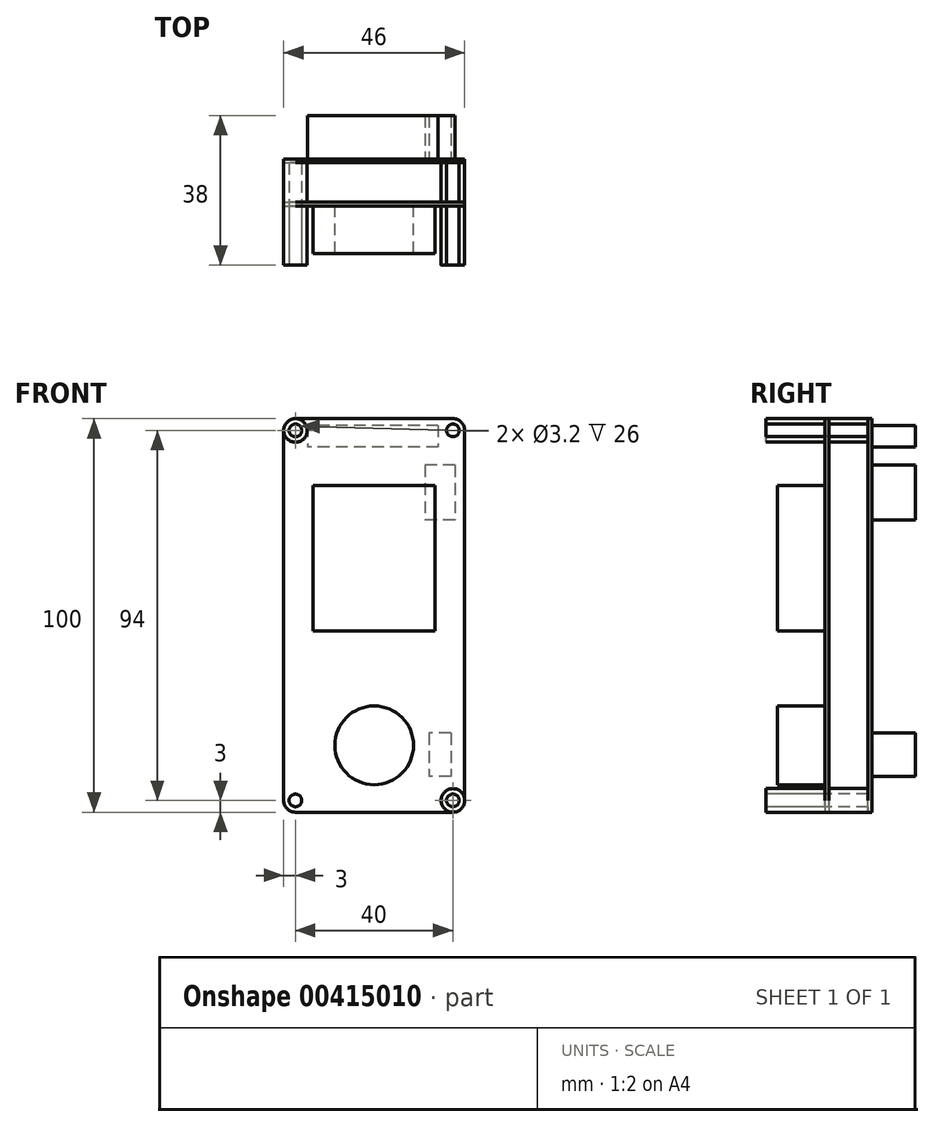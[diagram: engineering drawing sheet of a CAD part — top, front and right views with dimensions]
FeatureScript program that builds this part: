
annotation { "Feature Type Name" : "Feature", "Feature Type Description" : "" }
export const myFeature = defineFeature(function(context is Context, id is Id, definition is map)
    precondition{}
    {
        {
            var Q0;
            Q0=qCreatedBy(makeId("Front.planeOp"),FACE);
            var sketch = newSketch(context, id + "F0", { "sketchPlane" : qUnion([Q0])});
            skLineSegment(sketch, "E0.bottom", {"start": v(20, 50) * mm, "end": v(-20, 50) * mm});
            skLineSegment(sketch, "E0.top", {"start": v(20, -50) * mm, "end": v(-20, -50) * mm});
            skLineSegment(sketch, "E0.left", {"start": v(23, 47) * mm, "end": v(23, -47) * mm});
            skLineSegment(sketch, "E0.right", {"start": v(-23, 47) * mm, "end": v(-23, -47) * mm});
            skPoint(sketch, "E0.middle", {"position": v(0, 0) * mm});
            skPoint(sketch, "E1.visualSharp", {"position": v(-23, 50) * mm});
            skArc(sketch, "E1.filletArc", {"start": v(-20, 50) * mm, "mid": v(-22.12, 49.12) * mm, "end": v(-23, 47) * mm});
            skPoint(sketch, "E2.visualSharp", {"position": v(23, 50) * mm});
            skArc(sketch, "E2.filletArc", {"start": v(23, 47) * mm, "mid": v(22.12, 49.12) * mm, "end": v(20, 50) * mm});
            skPoint(sketch, "E3.visualSharp", {"position": v(23, -50) * mm});
            skArc(sketch, "E3.filletArc", {"start": v(20, -50) * mm, "mid": v(22.12, -49.12) * mm, "end": v(23, -47) * mm});
            skPoint(sketch, "E4.visualSharp", {"position": v(-23, -50) * mm});
            skArc(sketch, "E4.filletArc", {"start": v(-23, -47) * mm, "mid": v(-22.12, -49.12) * mm, "end": v(-20, -50) * mm});
            skCircle(sketch, "E5", {"center": v(-20, 47) * mm, "radius": 1.6 * mm});
            skCircle(sketch, "E6.MirrorC", {"center": v(20, 47) * mm, "radius": 1.6 * mm});
            skCircle(sketch, "E7.MirrorC", {"center": v(-20, -47) * mm, "radius": 1.6 * mm});
            skCircle(sketch, "E8.MirrorC", {"center": v(20, -47) * mm, "radius": 1.6 * mm});
            skLineSegment(sketch, "E9.bottom", {"start": v(-15.5, 33) * mm, "end": v(15.5, 33) * mm});
            skLineSegment(sketch, "E9.top", {"start": v(-15.5, -4) * mm, "end": v(15.5, -4) * mm});
            skLineSegment(sketch, "E9.left", {"start": v(-15.5, 33) * mm, "end": v(-15.5, -4) * mm});
            skLineSegment(sketch, "E9.right", {"start": v(15.5, 33) * mm, "end": v(15.5, -4) * mm});
            skPoint(sketch, "E9.middle", {"position": v(0, 14.5) * mm});
            skCircle(sketch, "E10", {"center": v(0, -33) * mm, "radius": 10 * mm});
            skSolve(sketch);
        }
        {
            var Q0;
            Q0=makeQuery(id+"F0.imprint","IMPRINT",FACE,{"disambiguationData":[TD([[makeQuery(id+"F0.imprint","IMPRINT",EDGE,{"derivedFrom":sQuery(id+"F0.wireOp",EDGE,"E0.bottom")}),1.0]])]});
            var Q1;
            Q1=makeQuery(id+"F0.imprint","IMPRINT",FACE,{"disambiguationData":[TD([[makeQuery(id+"F0.imprint","IMPRINT",EDGE,{"derivedFrom":sQuery(id+"F0.wireOp",EDGE,"E9.bottom")}),-1.0]])]});
            var Q2;
            Q2=makeQuery(id+"F0.imprint","IMPRINT",FACE,{"disambiguationData":[TD([[makeQuery(id+"F0.imprint","IMPRINT",EDGE,{"derivedFrom":sQuery(id+"F0.wireOp",EDGE,"E10")}),1.0]])]});
            extrude(context, id + "F1", {"entities" : qUnion([Q0, Q1, Q2]), "oppositeDirection" : true, "depth" : 1 * mm});
        }
        {
            var Q0;
            Q0=makeQuery(id+"F0.imprint","IMPRINT",FACE,{"disambiguationData":[TD([[makeQuery(id+"F0.imprint","IMPRINT",EDGE,{"derivedFrom":sQuery(id+"F0.wireOp",EDGE,"E9.bottom")}),-1.0]])]});
            var Q1;
            Q1=makeQuery(id+"F0.imprint","IMPRINT",FACE,{"disambiguationData":[TD([[makeQuery(id+"F0.imprint","IMPRINT",EDGE,{"derivedFrom":sQuery(id+"F0.wireOp",EDGE,"E10")}),1.0]])]});
            extrude(context, id + "F2", {"entities" : qUnion([Q0, Q1]), "operationType" : NewBodyOperationType.ADD, "depth" : 12 * mm});
        }
        {
            var Q0;
            Q0=makeQuery(id+"F1.opExtrude","CAP_FACE",FACE,{"disambiguationData":[OSD([sQuery(id+"F0.wireOp",EDGE,"E0.bottom"),sQuery(id+"F0.wireOp",EDGE,"E0.top"),sQuery(id+"F0.wireOp",EDGE,"E0.left"),sQuery(id+"F0.wireOp",EDGE,"E0.right"),sQuery(id+"F0.wireOp",EDGE,"E1.filletArc"),sQuery(id+"F0.wireOp",EDGE,"E2.filletArc"),sQuery(id+"F0.wireOp",EDGE,"E3.filletArc"),sQuery(id+"F0.wireOp",EDGE,"E4.filletArc"),sQuery(id+"F0.wireOp",EDGE,"E5"),sQuery(id+"F0.wireOp",EDGE,"E6.MirrorC"),sQuery(id+"F0.wireOp",EDGE,"E7.MirrorC"),sQuery(id+"F0.wireOp",EDGE,"E8.MirrorC")])],"isStart":false});
            var sketch = newSketch(context, id + "F3", { "sketchPlane" : qUnion([Q0])});
            skCircle(sketch, "E11.0", {"center": v(-20, 47) * mm, "radius": 1.6 * mm});
            skArc(sketch, "E12.0", {"start": v(-23, 47) * mm, "mid": v(-22.12, 49.12) * mm, "end": v(-20, 50) * mm});
            skCircle(sketch, "E13.0", {"center": v(20, 47) * mm, "radius": 1.6 * mm});
            skArc(sketch, "E14.0", {"start": v(20, 50) * mm, "mid": v(22.12, 49.12) * mm, "end": v(23, 47) * mm});
            skCircle(sketch, "E15.0", {"center": v(20, -47) * mm, "radius": 1.6 * mm});
            skArc(sketch, "E16.0", {"start": v(23, -47) * mm, "mid": v(22.12, -49.12) * mm, "end": v(20, -50) * mm});
            skCircle(sketch, "E17.0", {"center": v(-20, -47) * mm, "radius": 1.6 * mm});
            skArc(sketch, "E18.0", {"start": v(-20, -50) * mm, "mid": v(-22.12, -49.12) * mm, "end": v(-23, -47) * mm});
            skCircle(sketch, "E19", {"center": v(-20, -47) * mm, "radius": 3 * mm});
            skCircle(sketch, "E20", {"center": v(20, -47) * mm, "radius": 3 * mm});
            skCircle(sketch, "E21", {"center": v(-20, 47) * mm, "radius": 3 * mm});
            skCircle(sketch, "E22", {"center": v(20, 47) * mm, "radius": 3 * mm});
            skSolve(sketch);
        }
        {
            var Q0;
            Q0=makeQuery(id+"F3.imprint","IMPRINT",FACE,{"disambiguationData":[TD([[makeQuery(id+"F3.imprint","IMPRINT",EDGE,{"derivedFrom":sQuery(id+"F3.wireOp",EDGE,"E11.0")}),-1.0]])]});
            var Q1;
            Q1=makeQuery(id+"F3.imprint","IMPRINT",FACE,{"disambiguationData":[TD([[makeQuery(id+"F3.imprint","IMPRINT",EDGE,{"derivedFrom":sQuery(id+"F3.wireOp",EDGE,"E13.0")}),1.0]])]});
            var Q2;
            Q2=makeQuery(id+"F3.imprint","IMPRINT",FACE,{"disambiguationData":[TD([[makeQuery(id+"F3.imprint","IMPRINT",EDGE,{"derivedFrom":sQuery(id+"F3.wireOp",EDGE,"E15.0")}),-1.0]])]});
            var Q3;
            Q3=makeQuery(id+"F3.imprint","IMPRINT",FACE,{"disambiguationData":[TD([[makeQuery(id+"F3.imprint","IMPRINT",EDGE,{"derivedFrom":sQuery(id+"F3.wireOp",EDGE,"E17.0")}),1.0]])]});
            extrude(context, id + "F4", {"entities" : qUnion([Q0, Q1, Q2, Q3]), "operationType" : NewBodyOperationType.ADD, "depth" : 10 * mm});
        }
        {
            var Q0;
            Q0=makeQuery(id+"F3.imprint","IMPRINT",FACE,{"disambiguationData":[TD([[makeQuery(id+"F3.imprint","IMPRINT",EDGE,{"derivedFrom":sQuery(id+"F3.wireOp",EDGE,"E11.0")}),-1.0]])]});
            var Q1;
            Q1=makeQuery(id+"F3.imprint","IMPRINT",FACE,{"disambiguationData":[TD([[makeQuery(id+"F3.imprint","IMPRINT",EDGE,{"derivedFrom":sQuery(id+"F3.wireOp",EDGE,"E17.0")}),1.0]])]});
            var Q2;
            Q2=makeQuery(id+"F3.imprint","IMPRINT",FACE,{"disambiguationData":[TD([[makeQuery(id+"F3.imprint","IMPRINT",EDGE,{"derivedFrom":sQuery(id+"F3.wireOp",EDGE,"E15.0")}),-1.0]])]});
            var Q3;
            Q3=makeQuery(id+"F3.imprint","IMPRINT",FACE,{"disambiguationData":[TD([[makeQuery(id+"F3.imprint","IMPRINT",EDGE,{"derivedFrom":sQuery(id+"F3.wireOp",EDGE,"E13.0")}),1.0]])]});
            extrude(context, id + "F5", {"entities" : qUnion([Q0, Q1, Q2, Q3]), "operationType" : NewBodyOperationType.ADD, "oppositeDirection" : true, "depth" : 16 * mm});
        }
        {
            var Q0;
            Q0=makeQuery(id+"F4.opExtrude","CAP_FACE",FACE,{"disambiguationData":[OSD([sQuery(id+"F3.wireOp",EDGE,"E11.0"),sQuery(id+"F3.wireOp",EDGE,"E21")])],"isStart":false});
            var sketch = newSketch(context, id + "F6", { "sketchPlane" : qUnion([Q0])});
            skCircle(sketch, "E23.0", {"center": v(-20, 47) * mm, "radius": 3 * mm});
            skCircle(sketch, "E24.0", {"center": v(20, 47) * mm, "radius": 3 * mm});
            skCircle(sketch, "E25.0", {"center": v(20, -47) * mm, "radius": 3 * mm});
            skCircle(sketch, "E26.0", {"center": v(-20, -47) * mm, "radius": 3 * mm});
            skLineSegment(sketch, "E27", {"start": v(-23, 47) * mm, "end": v(-23, -47) * mm});
            skLineSegment(sketch, "E28", {"start": v(-20, -50) * mm, "end": v(20, -50) * mm});
            skLineSegment(sketch, "E29", {"start": v(23, -47) * mm, "end": v(23, 47) * mm});
            skLineSegment(sketch, "E30", {"start": v(20, 50) * mm, "end": v(-20, 50) * mm});
            skSolve(sketch);
        }
        {
            var Q0;
            {var subQ3=sQuery(id+"F6.wireOp",EDGE,"E27");Q0=makeQuery(id+"F6.imprint","IMPRINT",FACE,{"disambiguationData":[TD([[makeQuery(id+"F6.imprint","IMPRINT",EDGE,{"derivedFrom":subQ3}),1.0]])]});}
            var Q1;
            Q1=makeQuery(id+"F6.imprint","IMPRINT",FACE,{"disambiguationData":[TD([[makeQuery(id+"F6.imprint","IMPRINT",EDGE,{"derivedFrom":makeQuery(id+"F4.opExtrude","CAP_EDGE",EDGE,{"disambiguationData":[OSD([sQuery(id+"F3.wireOp",EDGE,"E11.0")])],"isStart":false})}),-1.0]])]});
            var Q2;
            {var subQ0=sQuery(id+"F6.wireOp",EDGE,"E24.0");var subQ1=makeQuery(id+"F6.imprint","INTERSECT",VERTEX,{"derivedFrom":[subQ0,sQuery(id+"F6.wireOp",EDGE,"E29")]});Q2=makeQuery(id+"F6.imprint","IMPRINT",FACE,{"disambiguationData":[TD([[makeQuery(id+"F6.imprint","IMPRINT",EDGE,{"disambiguationData":[TD([[subQ1,1.0]])],"derivedFrom":subQ0}),1.0]])]});}
            var Q3;
            {var subQ0=sQuery(id+"F6.wireOp",EDGE,"E26.0");var subQ1=makeQuery(id+"F6.imprint","INTERSECT",VERTEX,{"derivedFrom":[subQ0,sQuery(id+"F6.wireOp",EDGE,"E27")]});Q3=makeQuery(id+"F6.imprint","IMPRINT",FACE,{"disambiguationData":[TD([[makeQuery(id+"F6.imprint","IMPRINT",EDGE,{"disambiguationData":[TD([[subQ1,-1.0]])],"derivedFrom":subQ0}),1.0]])]});}
            var Q4;
            {var subQ0=sQuery(id+"F6.wireOp",EDGE,"E25.0");var subQ1=makeQuery(id+"F6.imprint","INTERSECT",VERTEX,{"derivedFrom":[subQ0,sQuery(id+"F6.wireOp",EDGE,"E28")]});Q4=makeQuery(id+"F6.imprint","IMPRINT",FACE,{"disambiguationData":[TD([[makeQuery(id+"F6.imprint","IMPRINT",EDGE,{"disambiguationData":[TD([[subQ1,-1.0]])],"derivedFrom":subQ0}),1.0]])]});}
            var Q5;
            Q5=makeQuery(id+"F6.imprint","IMPRINT",FACE,{"disambiguationData":[TD([[makeQuery(id+"F6.imprint","IMPRINT",EDGE,{"derivedFrom":makeQuery(id+"F4.opExtrude","CAP_EDGE",EDGE,{"disambiguationData":[OSD([sQuery(id+"F3.wireOp",EDGE,"E11.0")])],"isStart":false})}),1.0]])]});
            extrude(context, id + "F7", {"entities" : qUnion([Q0, Q1, Q2, Q3, Q4, Q5]), "operationType" : NewBodyOperationType.ADD, "depth" : 1 * mm});
        }
        {
            var Q0;
            Q0=makeQuery(id+"F7.opExtrude","CAP_FACE",FACE,{"disambiguationData":[OSD([sQuery(id+"F6.wireOp",EDGE,"E23.0"),sQuery(id+"F6.wireOp",EDGE,"E24.0"),sQuery(id+"F6.wireOp",EDGE,"E25.0"),sQuery(id+"F6.wireOp",EDGE,"E26.0"),sQuery(id+"F6.wireOp",EDGE,"E27"),sQuery(id+"F6.wireOp",EDGE,"E28"),sQuery(id+"F6.wireOp",EDGE,"E29"),sQuery(id+"F6.wireOp",EDGE,"E30")])],"isStart":false});
            var sketch = newSketch(context, id + "F8", { "sketchPlane" : qUnion([Q0])});
            skLineSegment(sketch, "E31.bottom", {"start": v(-16.25, 48.3) * mm, "end": v(16.97, 48.3) * mm});
            skLineSegment(sketch, "E31.top", {"start": v(-16.25, 42.76) * mm, "end": v(16.97, 42.76) * mm});
            skLineSegment(sketch, "E31.left", {"start": v(-16.25, 48.3) * mm, "end": v(-16.25, 42.76) * mm});
            skLineSegment(sketch, "E31.right", {"start": v(16.97, 48.3) * mm, "end": v(16.97, 42.76) * mm});
            skLineSegment(sketch, "E32.bottom", {"start": v(-20.52, 38.21) * mm, "end": v(-12.9, 38.21) * mm});
            skLineSegment(sketch, "E32.top", {"start": v(-20.52, 24.24) * mm, "end": v(-12.9, 24.24) * mm});
            skLineSegment(sketch, "E32.left", {"start": v(-20.52, 38.21) * mm, "end": v(-20.52, 24.24) * mm});
            skLineSegment(sketch, "E32.right", {"start": v(-12.9, 38.21) * mm, "end": v(-12.9, 24.24) * mm});
            skLineSegment(sketch, "E33.bottom", {"start": v(-19.48, -29.84) * mm, "end": v(-13.93, -29.84) * mm});
            skLineSegment(sketch, "E33.top", {"start": v(-19.48, -40.95) * mm, "end": v(-13.93, -40.95) * mm});
            skLineSegment(sketch, "E33.left", {"start": v(-19.48, -29.84) * mm, "end": v(-19.48, -40.95) * mm});
            skLineSegment(sketch, "E33.right", {"start": v(-13.93, -29.84) * mm, "end": v(-13.93, -40.95) * mm});
            skSolve(sketch);
        }
        {
            var Q0;
            Q0=makeQuery(id+"F8.imprint","IMPRINT",FACE,{"disambiguationData":[TD([[makeQuery(id+"F8.imprint","IMPRINT",EDGE,{"derivedFrom":sQuery(id+"F8.wireOp",EDGE,"E31.bottom")}),-1.0]])]});
            var Q1;
            Q1=makeQuery(id+"F8.imprint","IMPRINT",FACE,{"disambiguationData":[TD([[makeQuery(id+"F8.imprint","IMPRINT",EDGE,{"derivedFrom":sQuery(id+"F8.wireOp",EDGE,"E32.bottom")}),-1.0]])]});
            var Q2;
            Q2=makeQuery(id+"F8.imprint","IMPRINT",FACE,{"disambiguationData":[TD([[makeQuery(id+"F8.imprint","IMPRINT",EDGE,{"derivedFrom":sQuery(id+"F8.wireOp",EDGE,"E33.bottom")}),-1.0]])]});
            extrude(context, id + "F9", {"entities" : qUnion([Q0, Q1, Q2]), "operationType" : NewBodyOperationType.ADD, "depth" : 11 * mm});
        }
    });
